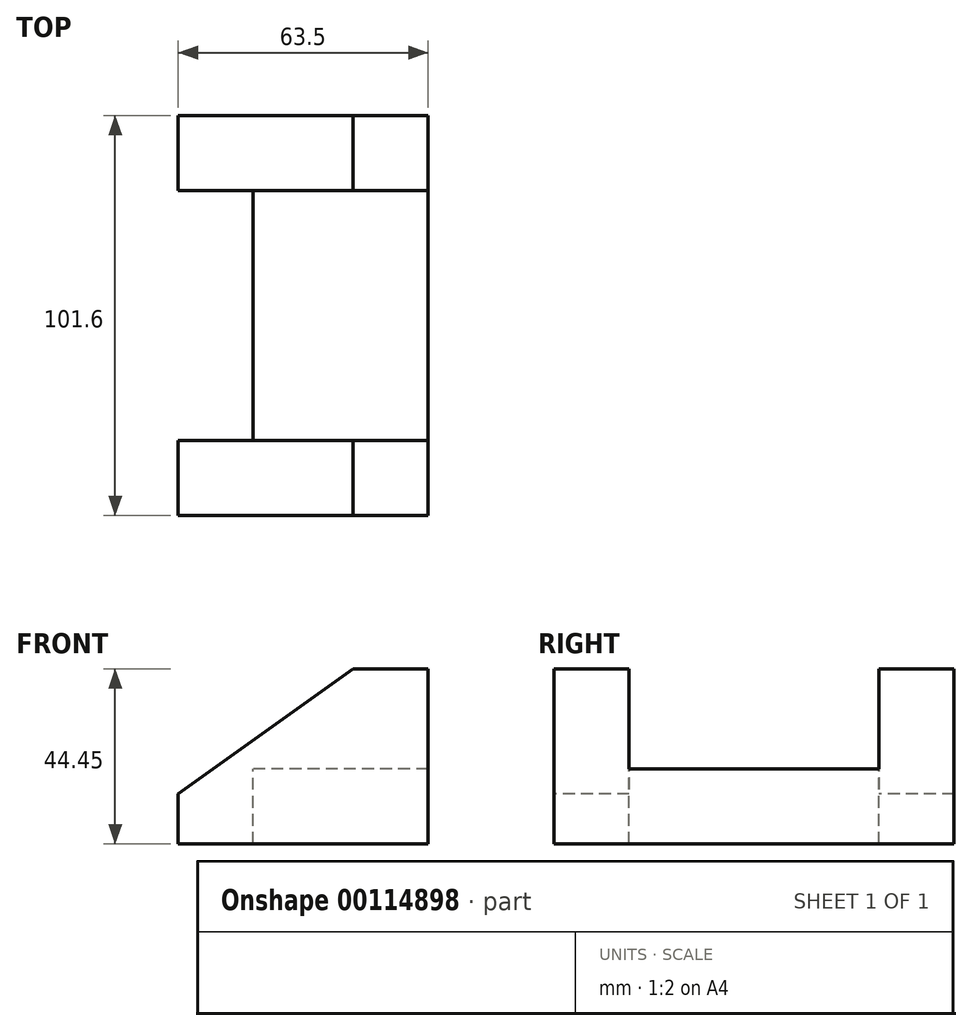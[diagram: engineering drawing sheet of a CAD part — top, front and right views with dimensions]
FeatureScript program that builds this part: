
annotation { "Feature Type Name" : "Feature", "Feature Type Description" : "" }
export const myFeature = defineFeature(function(context is Context, id is Id, definition is map)
    precondition{}
    {
        {
            var Q0;
            Q0=qCreatedBy(makeId("Front.planeOp"),FACE);
            var sketch = newSketch(context, id + "F0", { "sketchPlane" : qUnion([Q0])});
            skLineSegment(sketch, "E0", {"start": v(0, 0) * mm, "end": v(63.5, 0) * mm});
            skLineSegment(sketch, "E1", {"start": v(63.5, 0) * mm, "end": v(63.5, 44.45) * mm});
            skLineSegment(sketch, "E2", {"start": v(63.5, 44.45) * mm, "end": v(44.45, 44.45) * mm});
            skLineSegment(sketch, "E3", {"start": v(44.45, 44.45) * mm, "end": v(0, 12.7) * mm});
            skLineSegment(sketch, "E4", {"start": v(0, 0) * mm, "end": v(0, 12.7) * mm});
            skSolve(sketch);
        }
        {
            var Q0;
            Q0=makeQuery(id+"F0.imprint","IMPRINT",FACE,{"disambiguationData":[TD([[makeQuery(id+"F0.imprint","IMPRINT",EDGE,{"derivedFrom":sQuery(id+"F0.wireOp",EDGE,"E0")}),1.0]])]});
            extrude(context, id + "F1", {"entities" : qUnion([Q0]), "oppositeDirection" : true, "depth" : 19.05 * mm});
        }
        {
            var Q0;
            Q0=makeQuery(id+"F1.opExtrude","CAP_FACE",FACE,{"disambiguationData":[OSD([sQuery(id+"F0.wireOp",EDGE,"E0"),sQuery(id+"F0.wireOp",EDGE,"E1"),sQuery(id+"F0.wireOp",EDGE,"E2"),sQuery(id+"F0.wireOp",EDGE,"E3"),sQuery(id+"F0.wireOp",EDGE,"E4")])],"isStart":false});
            var sketch = newSketch(context, id + "F2", { "sketchPlane" : qUnion([Q0])});
            skLineSegment(sketch, "E5.bottom", {"start": v(-63.5, 0) * mm, "end": v(-19.05, 0) * mm});
            skLineSegment(sketch, "E5.top", {"start": v(-63.5, 19.05) * mm, "end": v(-19.05, 19.05) * mm});
            skLineSegment(sketch, "E5.left", {"start": v(-63.5, 0) * mm, "end": v(-63.5, 19.05) * mm});
            skLineSegment(sketch, "E5.right", {"start": v(-19.05, 0) * mm, "end": v(-19.05, 19.05) * mm});
            skSolve(sketch);
        }
        {
            var Q0;
            Q0 = qSketchRegion(id + "F2", true);
            extrude(context, id + "F3", {"entities" : qUnion([Q0]), "operationType" : NewBodyOperationType.ADD, "depth" : 63.5 * mm});
        }
        {
            var Q0;
            Q0=makeQuery(id+"F3.opExtrude","CAP_FACE",FACE,{"disambiguationData":[OSD([sQuery(id+"F2.wireOp",EDGE,"E5.bottom"),sQuery(id+"F2.wireOp",EDGE,"E5.top"),sQuery(id+"F2.wireOp",EDGE,"E5.left"),sQuery(id+"F2.wireOp",EDGE,"E5.right")])],"isStart":false});
            var sketch = newSketch(context, id + "F4", { "sketchPlane" : qUnion([Q0])});
            skLineSegment(sketch, "E6", {"start": v(-63.5, 0) * mm, "end": v(-63.5, 44.45) * mm});
            skLineSegment(sketch, "E7", {"start": v(-63.5, 44.45) * mm, "end": v(-44.45, 44.45) * mm});
            skLineSegment(sketch, "E8", {"start": v(-44.45, 44.45) * mm, "end": v(0, 12.7) * mm});
            skLineSegment(sketch, "E9", {"start": v(0, 0) * mm, "end": v(0, 12.7) * mm});
            skLineSegment(sketch, "E10", {"start": v(0, 0) * mm, "end": v(-63.5, 0) * mm});
            skSolve(sketch);
        }
        {
            var Q0;
            {var subQ3=sQuery(id+"F4.wireOp",EDGE,"E7");Q0=makeQuery(id+"F4.imprint","IMPRINT",FACE,{"disambiguationData":[TD([[makeQuery(id+"F4.imprint","IMPRINT",EDGE,{"derivedFrom":subQ3}),-1.0]])]});}
            var Q1;
            {var subQ3=makeQuery(id+"F3.opExtrude","CAP_EDGE",EDGE,{"disambiguationData":[OSD([sQuery(id+"F2.wireOp",EDGE,"E5.top")])],"isStart":false});Q1=makeQuery(id+"F4.imprint","IMPRINT",FACE,{"disambiguationData":[TD([[makeQuery(id+"F4.imprint","IMPRINT",EDGE,{"derivedFrom":subQ3}),-1.0]])]});}
            extrude(context, id + "F5", {"entities" : qUnion([Q0, Q1]), "operationType" : NewBodyOperationType.ADD, "depth" : 19.05 * mm});
        }
    });
